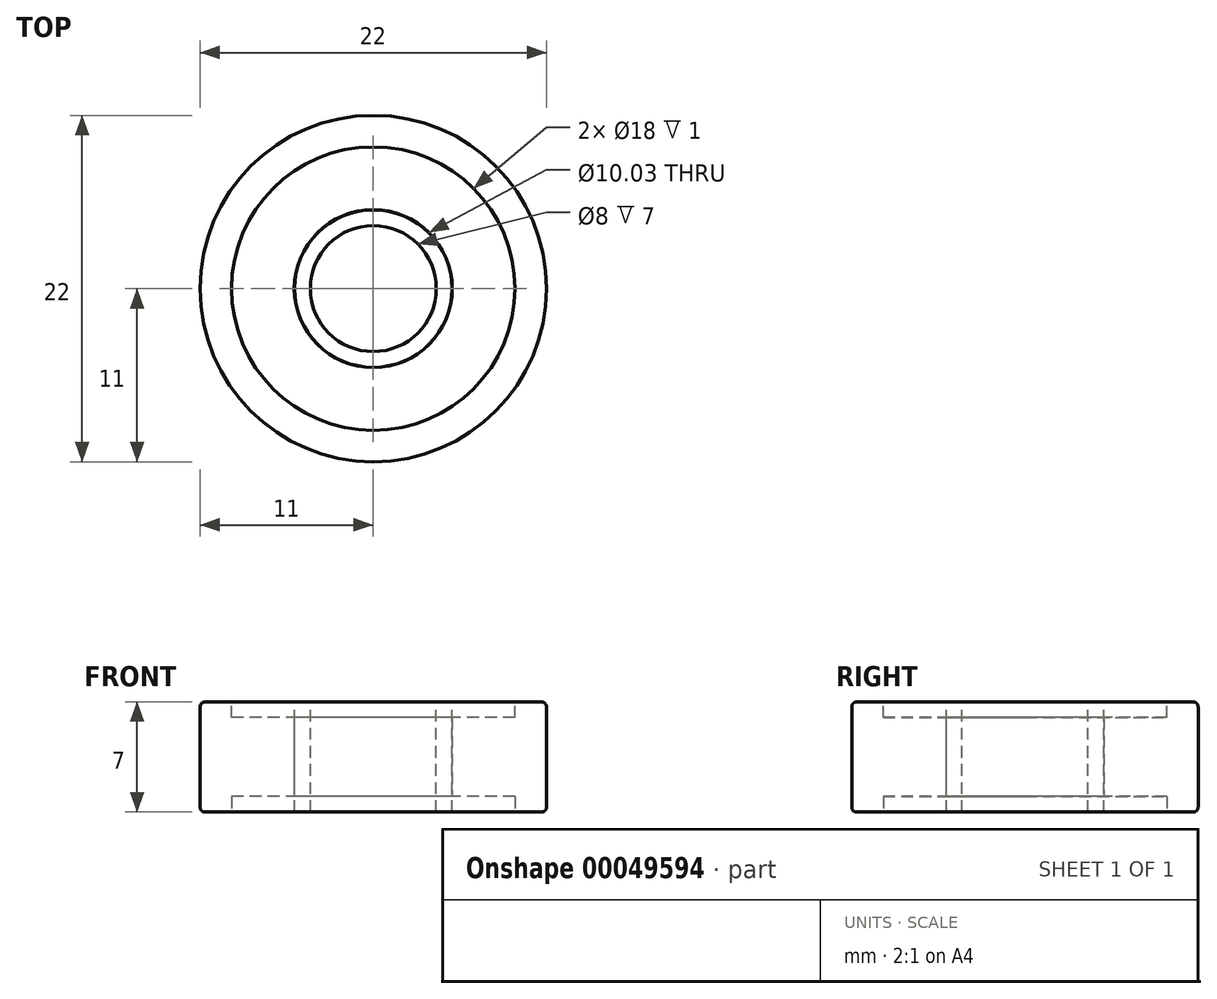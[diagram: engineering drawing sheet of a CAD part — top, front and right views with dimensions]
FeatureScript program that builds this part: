
annotation { "Feature Type Name" : "Feature", "Feature Type Description" : "" }
export const myFeature = defineFeature(function(context is Context, id is Id, definition is map)
    precondition{}
    {
        {
            var Q0;
            Q0=qCreatedBy(makeId("Top.planeOp"),FACE);
            var sketch = newSketch(context, id + "F0", { "sketchPlane" : qUnion([Q0])});
            skCircle(sketch, "E0", {"center": v(0, 0) * mm, "radius": 11 * mm});
            skSolve(sketch);
        }
        {
            var Q0;
            Q0 = qSketchRegion(id + "F0", true);
            extrude(context, id + "F1", {"entities" : qUnion([Q0]), "depth" : 3.5 * mm});
        }
        {
            var Q0;
            Q0=makeQuery(id+"F1.opExtrude","CAP_FACE",FACE,{"disambiguationData":[OSD([sQuery(id+"F0.wireOp",EDGE,"E0")])],"isStart":false});
            var sketch = newSketch(context, id + "F2", { "sketchPlane" : qUnion([Q0])});
            skCircle(sketch, "E1", {"center": v(0, 0) * mm, "radius": 9 * mm});
            skCircle(sketch, "E2", {"center": v(0, 0) * mm, "radius": 5 * mm});
            skSolve(sketch);
        }
        {
            var Q0;
            Q0 = qSketchRegion(id + "F2", true);
            var Q1;
            Q1=makeQuery(id+"F1.opExtrude","CAP_FACE",FACE,{"disambiguationData":[OSD([sQuery(id+"F0.wireOp",EDGE,"E0")])],"isStart":true});
            extrude(context, id + "F3", {"entities" : qUnion([Q0]), "operationType" : NewBodyOperationType.REMOVE, "endBound" : BoundingType.UP_TO_SURFACE, "oppositeDirection" : true, "endBoundEntityFace" : qUnion([Q1]), "depth" : 25.4 * mm});
        }
        {
            var Q0;
            Q0=makeQuery(id+"F3.boolean.opBoolean","SPLIT",FACE,{"disambiguationData":[TD([makeQuery(id+"F3.opExtrude","SWEPT_FACE",FACE,{"disambiguationData":[OSD([sQuery(id+"F2.wireOp",EDGE,"E2")])]})])],"derivedFrom":makeQuery(id+"F1.opExtrude","CAP_FACE",FACE,{"disambiguationData":[OSD([sQuery(id+"F0.wireOp",EDGE,"E0")])],"isStart":false})});
            var sketch = newSketch(context, id + "F4", { "sketchPlane" : qUnion([Q0])});
            skPoint(sketch, "E3", {"position": v(0, 0) * mm});
            skSolve(sketch);
        }
        {
            var Q0;
            Q0=sQuery(id+"F4.wireOp",VERTEX,"E3");
            var Q1;
            Q1=makeQuery(id+"F3.boolean.opBoolean","SPLIT",BODY,{"disambiguationData":[OD(1.0)],"derivedFrom":makeQuery(id+"F1.opExtrude","SWEPT_BODY",BODY,{"disambiguationData":[OSD([sQuery(id+"F0.wireOp",EDGE,"E0")])]})});
            hole(context, id + "F5", {"style" : HoleStyle.SIMPLE, "holeDiameter" : 8 * mm, "endStyle" : HoleEndStyle.THROUGH, "locations" : qUnion([Q0]), "scope" : qUnion([Q1])});
        }
        {
            var Q0;
            Q0=qCreatedBy(makeId("Top.planeOp"),FACE);
            var sketch = newSketch(context, id + "F6", { "sketchPlane" : qUnion([Q0])});
            skCircle(sketch, "E4", {"center": v(0, 0) * mm, "radius": 9.05 * mm});
            skCircle(sketch, "E5", {"center": v(0, 0) * mm, "radius": 5.02 * mm});
            skSolve(sketch);
        }
        {
            var Q0;
            Q0 = qSketchRegion(id + "F6", true);
            extrude(context, id + "F7", {"entities" : qUnion([Q0]), "operationType" : NewBodyOperationType.ADD, "depth" : 2.5 * mm});
        }
        {
            var Q0;
            Q0=makeQuery(id+"F1.opExtrude","CAP_EDGE",EDGE,{"disambiguationData":[OSD([sQuery(id+"F0.wireOp",EDGE,"E0")])],"isStart":false});
            fillet(context, id + "F8", {"entities" : qUnion([Q0]), "radius" : 0.32 * mm, "tangentPropagation" : true, "allowEdgeOverflow" : false});
        }
        {
            var Q0;
            Q0=makeQuery(id+"F3.boolean.opBoolean","SPLIT",BODY,{"disambiguationData":[OD(0.0)],"derivedFrom":makeQuery(id+"F1.opExtrude","SWEPT_BODY",BODY,{"disambiguationData":[OSD([sQuery(id+"F0.wireOp",EDGE,"E0")])]})});
            var Q1;
            Q1=makeQuery(id+"F3.boolean.opBoolean","SPLIT",BODY,{"disambiguationData":[OD(1.0)],"derivedFrom":makeQuery(id+"F1.opExtrude","SWEPT_BODY",BODY,{"disambiguationData":[OSD([sQuery(id+"F0.wireOp",EDGE,"E0")])]})});
            var Q2;
            Q2=qCreatedBy(makeId("Top.planeOp"),FACE);
            mirror(context, id + "F9", {"operationType" : NewBodyOperationType.ADD, "entities" : qUnion([Q0, Q1]), "mirrorPlane" : qUnion([Q2])});
        }
    });
